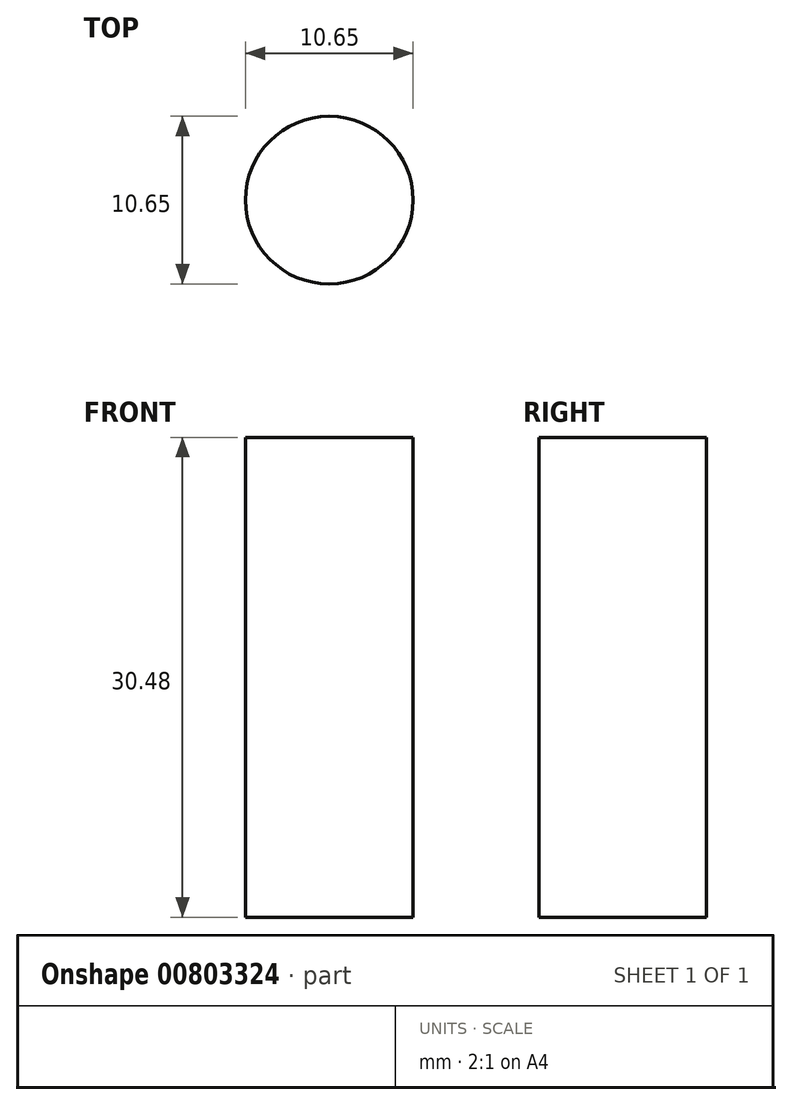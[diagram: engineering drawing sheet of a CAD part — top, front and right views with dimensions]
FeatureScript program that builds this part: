
annotation { "Feature Type Name" : "Feature", "Feature Type Description" : "" }
export const myFeature = defineFeature(function(context is Context, id is Id, definition is map)
    precondition{}
    {
        {
            var Q0;
            Q0=qCreatedBy(makeId("Top.planeOp"),FACE);
            var sketch = newSketch(context, id + "F0", { "sketchPlane" : qUnion([Q0])});
            skCircle(sketch, "E0", {"center": v(9.36, -10.15) * mm, "radius": 5.32 * mm});
            skSolve(sketch);
        }
        {
            var Q0;
            Q0=makeQuery(id+"F0.imprint","IMPRINT",FACE,{"disambiguationData":[TD([[makeQuery(id+"F0.imprint","IMPRINT",EDGE,{"derivedFrom":sQuery(id+"F0.wireOp",EDGE,"E0")}),1.0]])]});
            extrude(context, id + "F1", {"entities" : qUnion([Q0]), "depth" : 30.48 * mm, "offsetDistance" : 25.4 * mm});
        }
    });
